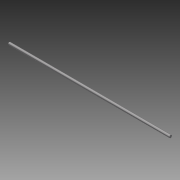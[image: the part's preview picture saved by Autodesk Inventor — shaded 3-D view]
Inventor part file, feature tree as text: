
AUTODESK INVENTOR PART (.ipt)
format: ipt  version: 2015 SP1 (Build 190203100, 203)  size: 84,480 bytes
history: native  units: in
note: dims shown in document units (in); Inventor stores cm internally (conversion verified against a paired STEP export)
features: extrude x1, sketch x1
ambient origin geometry x8: Origin, YZ Plane, XZ Plane, XY Plane, X Axis, Y Axis, Z Axis, Center Point
bodies: Solid1 (feature_tree)
feature tree (2):
  extrude  "Extrusion1"  Depth=23.0in TaperAngle=0.0deg
  sketch  "Sketch1"  dims[d0=0.375in d1=23.0in d2=0.0in]
